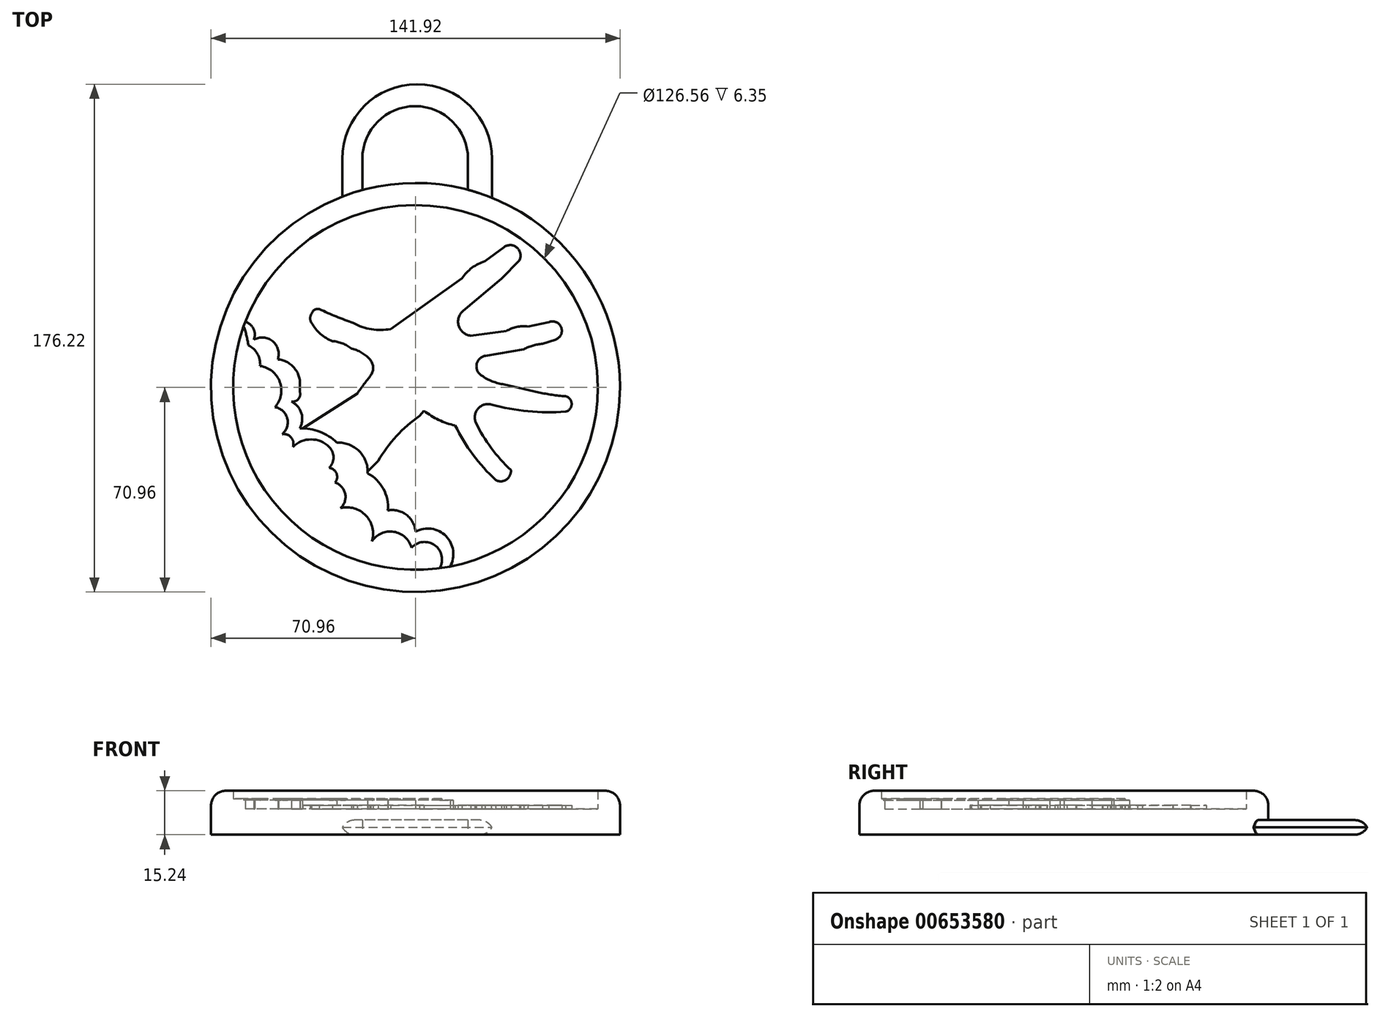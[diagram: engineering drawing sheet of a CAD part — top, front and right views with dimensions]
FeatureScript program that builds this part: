
annotation { "Feature Type Name" : "Feature", "Feature Type Description" : "" }
export const myFeature = defineFeature(function(context is Context, id is Id, definition is map)
    precondition{}
    {
        {
            var Q0;
            Q0=qCreatedBy(makeId("Top.planeOp"),FACE);
            var sketch = newSketch(context, id + "F0", { "sketchPlane" : qUnion([Q0])});
            skCircle(sketch, "E0", {"center": v(0, 0) * mm, "radius": 70.52 * mm});
            skSolve(sketch);
        }
        {
            var Q0;
            Q0=qCreatedBy(makeId("Top.planeOp"),FACE);
            var sketch = newSketch(context, id + "F1", { "sketchPlane" : qUnion([Q0])});
            skLineSegment(sketch, "E1", {"start": v(-43.52, -17) * mm, "end": v(-20.2, -2.1) * mm});
            skArc(sketch, "E2", {"start": v(-15.43, 4.3) * mm, "mid": v(-14.74, 7.14) * mm, "end": v(-15.89, 9.82) * mm});
            skArc(sketch, "E3", {"start": v(-15.89, 9.82) * mm, "mid": v(-18.77, 12.13) * mm, "end": v(-22.2, 13.5) * mm});
            skArc(sketch, "E4", {"start": v(-22.2, 13.5) * mm, "mid": v(-25.33, 15.28) * mm, "end": v(-28.82, 16.1) * mm});
            skArc(sketch, "E5", {"start": v(-36.02, 22.38) * mm, "mid": v(-33, 18.59) * mm, "end": v(-28.82, 16.1) * mm});
            skArc(sketch, "E6", {"start": v(-36.02, 25.57) * mm, "mid": v(-36.56, 23.98) * mm, "end": v(-36.02, 22.38) * mm});
            skArc(sketch, "E7", {"start": v(-33.37, 27.2) * mm, "mid": v(-35.03, 26.93) * mm, "end": v(-36.02, 25.57) * mm});
            skArc(sketch, "E8", {"start": v(-33.37, 27.2) * mm, "mid": v(-27.52, 24.63) * mm, "end": v(-21.53, 22.38) * mm});
            skArc(sketch, "E9", {"start": v(-21.53, 22.38) * mm, "mid": v(-15.27, 20.18) * mm, "end": v(-8.63, 20.3) * mm});
            skLineSegment(sketch, "E10", {"start": v(-8.63, 20.3) * mm, "end": v(7.57, 31.79) * mm});
            skLineSegment(sketch, "E11", {"start": v(7.57, 31.79) * mm, "end": v(16.12, 37.85) * mm});
            skArc(sketch, "E12", {"start": v(24.11, 43.84) * mm, "mid": v(19.6, 41.52) * mm, "end": v(16.12, 37.85) * mm});
            skLineSegment(sketch, "E13", {"start": v(24.11, 43.84) * mm, "end": v(30.69, 48.7) * mm});
            skArc(sketch, "E14", {"start": v(36.04, 44.15) * mm, "mid": v(35.17, 48.55) * mm, "end": v(30.69, 48.7) * mm});
            skLineSegment(sketch, "E15", {"start": v(36.04, 44.15) * mm, "end": v(29.83, 37.73) * mm});
            skLineSegment(sketch, "E16", {"start": v(29.83, 37.73) * mm, "end": v(16.53, 26.6) * mm});
            skArc(sketch, "E17", {"start": v(16.53, 26.6) * mm, "mid": v(15, 21.43) * mm, "end": v(19.16, 18) * mm});
            skLineSegment(sketch, "E18", {"start": v(19.16, 18) * mm, "end": v(31.48, 19.56) * mm});
            skArc(sketch, "E19", {"start": v(38.94, 21.18) * mm, "mid": v(35.07, 21.01) * mm, "end": v(31.48, 19.56) * mm});
            skLineSegment(sketch, "E20", {"start": v(38.94, 21.18) * mm, "end": v(46.2, 22.62) * mm});
            skArc(sketch, "E21", {"start": v(48.55, 16.61) * mm, "mid": v(50.56, 20.86) * mm, "end": v(46.2, 22.62) * mm});
            skLineSegment(sketch, "E22", {"start": v(48.55, 16.61) * mm, "end": v(44.1, 15.16) * mm});
            skLineSegment(sketch, "E23", {"start": v(37.61, 13.3) * mm, "end": v(24.2, 10.96) * mm});
            skArc(sketch, "E24", {"start": v(24.2, 10.96) * mm, "mid": v(21.2, 7.96) * mm, "end": v(23, 4.1) * mm});
            skArc(sketch, "E25", {"start": v(44.1, 15.16) * mm, "mid": v(40.76, 14.56) * mm, "end": v(37.61, 13.3) * mm});
            skArc(sketch, "E26", {"start": v(23, 4.1) * mm, "mid": v(26.67, 2.1) * mm, "end": v(30.7, 1.06) * mm});
            skLineSegment(sketch, "E27", {"start": v(30.7, 1.06) * mm, "end": v(42.84, -1.7) * mm});
            skArc(sketch, "E28", {"start": v(42.84, -1.7) * mm, "mid": v(47.41, -2.56) * mm, "end": v(52.04, -3.07) * mm});
            skArc(sketch, "E29", {"start": v(52.04, -8.4) * mm, "mid": v(54.19, -5.73) * mm, "end": v(52.04, -3.07) * mm});
            skArc(sketch, "E30", {"start": v(26.27, -5.89) * mm, "mid": v(39.05, -8.25) * mm, "end": v(52.04, -8.4) * mm});
            skArc(sketch, "E31", {"start": v(26.27, -5.89) * mm, "mid": v(21.64, -7.42) * mm, "end": v(21, -12.25) * mm});
            skArc(sketch, "E32", {"start": v(21, -12.25) * mm, "mid": v(26.27, -21) * mm, "end": v(33.09, -28.61) * mm});
            skArc(sketch, "E33", {"start": v(13.75, -13.17) * mm, "mid": v(19.93, -23.3) * mm, "end": v(27.87, -32.14) * mm});
            skArc(sketch, "E34", {"start": v(27.87, -32.14) * mm, "mid": v(31.54, -31.96) * mm, "end": v(33.09, -28.61) * mm});
            skArc(sketch, "E35", {"start": v(1.44, -9.91) * mm, "mid": v(-6.65, -16.9) * mm, "end": v(-12.94, -25.54) * mm});
            skLineSegment(sketch, "E36", {"start": v(-12.94, -25.54) * mm, "end": v(-16.45, -29.06) * mm});
            skLineSegment(sketch, "E37", {"start": v(-35.76, -29.06) * mm, "end": v(-43.52, -17) * mm});
            skLineSegment(sketch, "E38", {"start": v(-35.76, -29.06) * mm, "end": v(-16.45, -29.06) * mm});
            skLineSegment(sketch, "E39", {"start": v(2.98, -8.09) * mm, "end": v(1.44, -9.91) * mm});
            skArc(sketch, "E40", {"start": v(-15.43, 4.3) * mm, "mid": v(-17.87, 1.14) * mm, "end": v(-20.2, -2.1) * mm});
            skArc(sketch, "E41", {"start": v(2.98, -8.09) * mm, "mid": v(8.07, -11.26) * mm, "end": v(13.75, -13.17) * mm});
            skSolve(sketch);
        }
        {
            var Q0;
            Q0=qCreatedBy(makeId("Top.planeOp"),FACE);
            var sketch = newSketch(context, id + "F2", { "sketchPlane" : qUnion([Q0])});
            skArc(sketch, "E42", {"start": v(-56.1, 16.6) * mm, "mid": v(-56.51, 20.9) * mm, "end": v(-60.25, 23.06) * mm});
            skArc(sketch, "E43", {"start": v(-47.8, 9.74) * mm, "mid": v(-49.58, 16.04) * mm, "end": v(-56.1, 16.6) * mm});
            skArc(sketch, "E44", {"start": v(-40.18, 0) * mm, "mid": v(-41.87, 6.53) * mm, "end": v(-47.8, 9.74) * mm});
            skArc(sketch, "E45", {"start": v(-43, -4.93) * mm, "mid": v(-40.58, -3.93) * mm, "end": v(-40.18, -1.35) * mm});
            skArc(sketch, "E46", {"start": v(-40.18, -14.19) * mm, "mid": v(-39.6, -8.95) * mm, "end": v(-43, -4.93) * mm});
            skArc(sketch, "E47", {"start": v(-27.3, -19.16) * mm, "mid": v(-33.21, -15.32) * mm, "end": v(-40.18, -14.19) * mm});
            skArc(sketch, "E48", {"start": v(-16.6, -29.82) * mm, "mid": v(-19.57, -22.1) * mm, "end": v(-27.3, -19.16) * mm});
            skArc(sketch, "E49", {"start": v(-9.62, -42.68) * mm, "mid": v(-11.14, -35.19) * mm, "end": v(-16.6, -29.82) * mm});
            skArc(sketch, "E50", {"start": v(0, -50.02) * mm, "mid": v(-3.16, -44.19) * mm, "end": v(-9.62, -42.68) * mm});
            skArc(sketch, "E51", {"start": v(10.9, -63.77) * mm, "mid": v(11.22, -52.32) * mm, "end": v(0, -50.02) * mm});
            skArc(sketch, "E52", {"start": v(-60.25, 23.06) * mm, "mid": v(-51.86, -42.63) * mm, "end": v(10.9, -63.77) * mm});
            skArc(sketch, "E53", {"start": v(-40.18, -1.35) * mm, "mid": v(-40.15, -0.68) * mm, "end": v(-40.18, 0) * mm});
            skSolve(sketch);
        }
        {
            var Q0;
            Q0=qCreatedBy(makeId("Top.planeOp"),FACE);
            var sketch = newSketch(context, id + "F3", { "sketchPlane" : qUnion([Q0])});
            skArc(sketch, "E54", {"start": v(-58, 14.6) * mm, "mid": v(-58.86, 18.77) * mm, "end": v(-60.25, 22.8) * mm});
            skArc(sketch, "E55", {"start": v(-53.91, 7.45) * mm, "mid": v(-54.85, 11.66) * mm, "end": v(-58, 14.6) * mm});
            skArc(sketch, "E56", {"start": v(-48.81, -6.83) * mm, "mid": v(-47.06, 1.85) * mm, "end": v(-53.91, 7.45) * mm});
            skArc(sketch, "E57", {"start": v(-46.26, -16.18) * mm, "mid": v(-44.52, -10.68) * mm, "end": v(-48.81, -6.83) * mm});
            skArc(sketch, "E58", {"start": v(-42.52, -20.6) * mm, "mid": v(-43.15, -17.34) * mm, "end": v(-46.26, -16.18) * mm});
            skArc(sketch, "E59", {"start": v(-29.94, -20.6) * mm, "mid": v(-36.23, -18.02) * mm, "end": v(-42.52, -20.6) * mm});
            skArc(sketch, "E60", {"start": v(-29.94, -27.91) * mm, "mid": v(-28.47, -24.26) * mm, "end": v(-29.94, -20.6) * mm});
            skArc(sketch, "E61", {"start": v(-27.9, -33.01) * mm, "mid": v(-27.42, -29.86) * mm, "end": v(-29.94, -27.91) * mm});
            skArc(sketch, "E62", {"start": v(-26.03, -41.85) * mm, "mid": v(-24.4, -36.9) * mm, "end": v(-27.9, -33.01) * mm});
            skArc(sketch, "E63", {"start": v(-15.15, -53.42) * mm, "mid": v(-17.2, -44.45) * mm, "end": v(-26.03, -41.85) * mm});
            skArc(sketch, "E64", {"start": v(-1.38, -55.63) * mm, "mid": v(-7.55, -50.07) * mm, "end": v(-15.15, -53.42) * mm});
            skArc(sketch, "E65", {"start": v(7.67, -63.72) * mm, "mid": v(7.2, -55.15) * mm, "end": v(-1.38, -55.63) * mm});
            skArc(sketch, "E66", {"start": v(-60.25, 22.8) * mm, "mid": v(-52.75, -41.22) * mm, "end": v(7.67, -63.72) * mm});
            skSolve(sketch);
        }
        {
            var Q0;
            Q0 = qSketchRegion(id + "F0", true);
            extrude(context, id + "F4", {"entities" : qUnion([Q0]), "depth" : 8.9 * mm, "offsetDistance" : 25.4 * mm});
        }
        {
            var Q0;
            Q0 = qSketchRegion(id + "F1", true);
            extrude(context, id + "F5", {"entities" : qUnion([Q0]), "operationType" : NewBodyOperationType.ADD, "depth" : 10.16 * mm, "offsetDistance" : 25.4 * mm});
        }
        {
            var Q0;
            Q0 = qSketchRegion(id + "F2", true);
            extrude(context, id + "F6", {"entities" : qUnion([Q0]), "operationType" : NewBodyOperationType.ADD, "depth" : 11.94 * mm, "offsetDistance" : 25.4 * mm});
        }
        {
            var Q0;
            Q0 = qSketchRegion(id + "F3", true);
            extrude(context, id + "F7", {"entities" : qUnion([Q0]), "operationType" : NewBodyOperationType.ADD, "depth" : 12.45 * mm, "offsetDistance" : 25.4 * mm});
        }
        {
            var Q0;
            Q0=qCreatedBy(makeId("Top.planeOp"),FACE);
            var sketch = newSketch(context, id + "F8", { "sketchPlane" : qUnion([Q0])});
            skCircle(sketch, "E67", {"center": v(0, 0) * mm, "radius": 63.28 * mm});
            skCircle(sketch, "E68", {"center": v(0, 0) * mm, "radius": 70.96 * mm});
            skSolve(sketch);
        }
        {
            var Q0;
            Q0 = qSketchRegion(id + "F8", true);
            extrude(context, id + "F9", {"entities" : qUnion([Q0]), "operationType" : NewBodyOperationType.ADD, "depth" : 15.24 * mm, "offsetDistance" : 25.4 * mm});
        }
        {
            var Q0;
            Q0=makeQuery(id+"F9.opExtrude","CAP_EDGE",EDGE,{"disambiguationData":[OSD([sQuery(id+"F8.wireOp",EDGE,"E68")])],"isStart":false});
            fillet(context, id + "F10", {"entities" : qUnion([Q0]), "radius" : 5.08 * mm, "tangentPropagation" : true, "allowEdgeOverflow" : false});
        }
        {
            var Q0;
            Q0=qCreatedBy(makeId("Top.planeOp"),FACE);
            var sketch = newSketch(context, id + "F11", { "sketchPlane" : qUnion([Q0])});
            skLineSegment(sketch, "E69", {"start": v(27.2, 43.12) * mm, "end": v(-26.07, 43.12) * mm});
            skLineSegment(sketch, "E70", {"start": v(-26.07, 79.3) * mm, "end": v(-26.07, 43.12) * mm});
            skLineSegment(sketch, "E71", {"start": v(27.2, 43.12) * mm, "end": v(27.2, 79.3) * mm});
            skArc(sketch, "E72", {"start": v(27.2, 79.3) * mm, "mid": v(0.56, 105.94) * mm, "end": v(-26.07, 79.3) * mm});
            skLineSegment(sketch, "E73", {"start": v(-18.45, 51.94) * mm, "end": v(-18.45, 79.3) * mm});
            skArc(sketch, "E74", {"start": v(18.2, 79.3) * mm, "mid": v(-0.12, 97.63) * mm, "end": v(-18.45, 79.3) * mm});
            skLineSegment(sketch, "E75", {"start": v(18.2, 79.3) * mm, "end": v(18.2, 51.94) * mm});
            skLineSegment(sketch, "E76", {"start": v(-18.45, 51.94) * mm, "end": v(18.2, 51.94) * mm});
            skSolve(sketch);
        }
        {
            var Q0;
            Q0 = qSketchRegion(id + "F11", true);
            extrude(context, id + "F12", {"entities" : qUnion([Q0]), "operationType" : NewBodyOperationType.ADD, "depth" : 5.08 * mm, "offsetDistance" : 25.4 * mm});
        }
        {
            var Q0;
            Q0=makeQuery(id+"F12.opExtrude","CAP_EDGE",EDGE,{"disambiguationData":[OSD([sQuery(id+"F11.wireOp",EDGE,"E72")])],"isStart":false});
            var Q1;
            Q1=makeQuery(id+"F12.opExtrude","CAP_EDGE",EDGE,{"disambiguationData":[OSD([sQuery(id+"F11.wireOp",EDGE,"E72")])],"isStart":true});
            fillet(context, id + "F13", {"entities" : qUnion([Q0, Q1]), "radius" : 5.08 * mm, "tangentPropagation" : true, "allowEdgeOverflow" : false});
        }
    });
